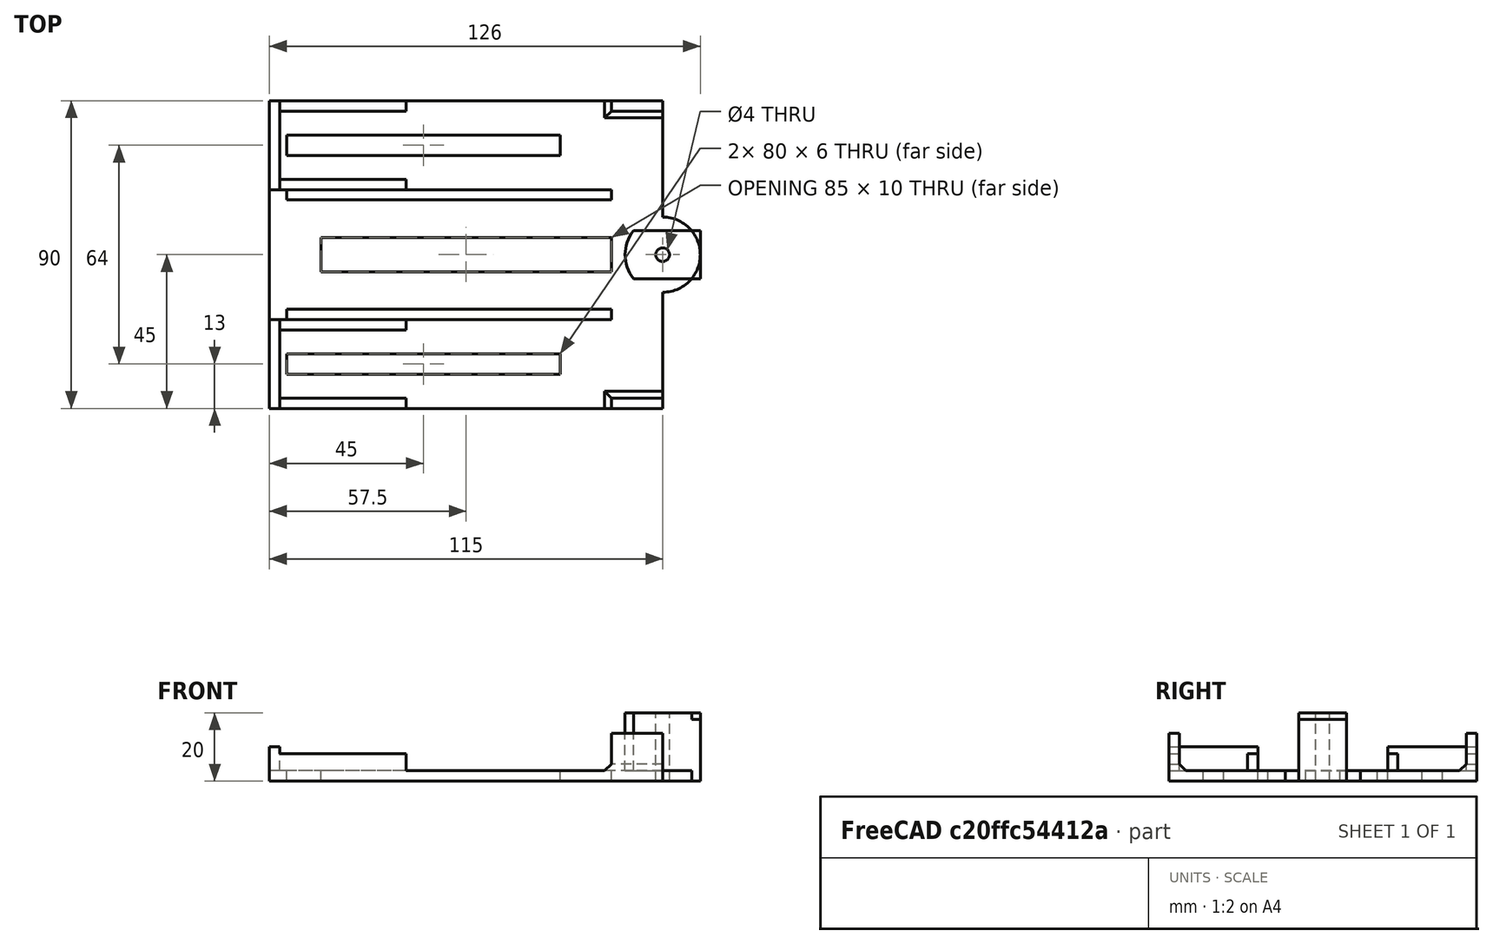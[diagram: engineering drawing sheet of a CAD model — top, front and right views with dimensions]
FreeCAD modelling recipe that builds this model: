
FCSTD DOCUMENT  (FreeCAD 0.18R16131 (Git))
Label: chassis_1
License: All rights reserved
LicenseURL: http://en.wikipedia.org/wiki/All_rights_reserved
objects: Part::Box×18, Part::MultiFuse×10, Part::Cut×9, Part::Cylinder×2, Part::Chamfer×2
note: 41 computed .brp shape members not serialized (recipe doc carries the construction recipe); baked Part::Feature solids carry a one-line shape summary decoded from their .brp

FEATURE [Part::Box] Box  label="Cube"
  AttacherType = Attacher::AttachEngine3D
  Height = 3
  Length = 115
  Width = 90
FEATURE [Part::Box] Box001  label="Cube001"
  AttacherType = Attacher::AttachEngine3D
  Height = 14
  Length = 15
  Placement = pos=(100,0,0) rot=(0,0,1;0rad)
  Width = 3
FEATURE [Part::MultiFuse] Fusion
  Shapes = -> [Box,Box001]
FEATURE [Part::Box] Box002  label="Cube002"
  AttacherType = Attacher::AttachEngine3D
  Height = 14
  Length = 15
  Placement = pos=(100,87,0) rot=(0,0,1;0rad)
  Width = 3
FEATURE [Part::MultiFuse] Fusion001
  Shapes = -> [Fusion,Box002]
FEATURE [Part::Cylinder] Cylinder
  Angle = 360
  AttacherType = Attacher::AttachEngine3D
  Height = 20
  Placement = pos=(115,45,0) rot=(0,0,1;0rad)
  Radius = 11
FEATURE [Part::MultiFuse] Fusion002
  Shapes = -> [Fusion001,Cylinder]
FEATURE [Part::Box] Box003  label="Cube003"
  AttacherType = Attacher::AttachEngine3D
  Height = 10
  Length = 3
  Width = 26
FEATURE [Part::MultiFuse] Fusion003
  Shapes = -> [Fusion002,Box003]
FEATURE [Part::Box] Box004  label="Cube004"
  AttacherType = Attacher::AttachEngine3D
  Height = 10
  Length = 3
  Placement = pos=(0,64,0) rot=(0,0,1;0rad)
  Width = 26
FEATURE [Part::MultiFuse] Fusion004
  Shapes = -> [Fusion003,Box004]
FEATURE [Part::Box] Box005  label="Cube005"
  AttacherType = Attacher::AttachEngine3D
  Height = 8
  Length = 40
  Width = 3
FEATURE [Part::MultiFuse] Fusion005
  Shapes = -> [Fusion004,Box005]
FEATURE [Part::Box] Box006  label="Cube006"
  AttacherType = Attacher::AttachEngine3D
  Height = 8
  Length = 40
  Placement = pos=(0,23,0) rot=(0,0,1;0rad)
  Width = 3
FEATURE [Part::MultiFuse] Fusion006
  Shapes = -> [Fusion005,Box006]
FEATURE [Part::Box] Box007  label="Cube007"
  AttacherType = Attacher::AttachEngine3D
  Height = 8
  Length = 40
  Placement = pos=(0,64,0) rot=(0,0,1;0rad)
  Width = 3
FEATURE [Part::MultiFuse] Fusion007
  Shapes = -> [Fusion006,Box007]
FEATURE [Part::Box] Box008  label="Cube008"
  AttacherType = Attacher::AttachEngine3D
  Height = 8
  Length = 40
  Placement = pos=(0,87,0) rot=(0,0,1;0rad)
  Width = 3
FEATURE [Part::MultiFuse] Fusion008
  Shapes = -> [Fusion007,Box008]
FEATURE [Part::Box] Box009  label="Cube009"
  AttacherType = Attacher::AttachEngine3D
  Height = 18
  Length = 10
  Placement = pos=(116,38,0) rot=(0,0,1;0rad)
  Width = 14
FEATURE [Part::MultiFuse] Fusion009
  Shapes = -> [Fusion008,Box009]
FEATURE [Part::Box] Box010  label="Cube010"
  AttacherType = Attacher::AttachEngine3D
  Height = 17
  Length = 21
  Placement = pos=(105,28,3) rot=(0,0,1;0rad)
  Width = 10
FEATURE [Part::Cut] Cut
  Base = -> Fusion009
  Tool = -> Box010
FEATURE [Part::Box] Box011  label="Cube011"
  AttacherType = Attacher::AttachEngine3D
  Height = 17
  Length = 21
  Placement = pos=(104,52,3) rot=(0,0,1;0rad)
  Width = 10
FEATURE [Part::Cut] Cut001
  Base = -> Cut
  Tool = -> Box011
FEATURE [Part::Box] Box012  label="Cube012"
  AttacherType = Attacher::AttachEngine3D
  Height = 10
  Length = 85
  Placement = pos=(20,40,0) rot=(0,0,1;0rad)
  Width = 10
FEATURE [Part::Cut] Cut002
  Base = -> Cut001
  Tool = -> Box012
FEATURE [Part::Box] Box013  label="Cube013"
  AttacherType = Attacher::AttachEngine3D
  Height = 10
  Length = 95
  Placement = pos=(5,26,0) rot=(0,0,1;0rad)
  Width = 3
FEATURE [Part::Cut] Cut003
  Base = -> Cut002
  Tool = -> Box013
FEATURE [Part::Box] Box014  label="Cube014"
  AttacherType = Attacher::AttachEngine3D
  Height = 10
  Length = 95
  Placement = pos=(5,61,0) rot=(0,0,1;0rad)
  Width = 3
FEATURE [Part::Cut] Cut004
  Base = -> Cut003
  Tool = -> Box014
FEATURE [Part::Box] Box015  label="Cube015"
  AttacherType = Attacher::AttachEngine3D
  Height = 10
  Length = 80
  Placement = pos=(5,10,0) rot=(0,0,1;0rad)
  Width = 6
FEATURE [Part::Cut] Cut005
  Base = -> Cut004
  Tool = -> Box015
FEATURE [Part::Box] Box016  label="Cube016"
  AttacherType = Attacher::AttachEngine3D
  Height = 10
  Length = 80
  Placement = pos=(5,74,0) rot=(0,0,1;0rad)
  Width = 6
FEATURE [Part::Cut] Cut006
  Base = -> Cut005
  Tool = -> Box016
FEATURE [Part::Chamfer] Chamfer
  Base = -> Cut006
  Edges = 2 edges r=2: [Edge179,Edge181]
FEATURE [Part::Chamfer] Chamfer001
  Base = -> Chamfer
  Edges = 2 edges r=2: [Edge24,Edge26]
FEATURE [Part::Box] Box017  label="Cube017"
  AttacherType = Attacher::AttachEngine3D
  Height = 10
  Length = 5
  Placement = pos=(15,40,0) rot=(0,0,1;0rad)
  Width = 10
FEATURE [Part::Cut] Cut007
  Base = -> Chamfer001
  Tool = -> Box017
FEATURE [Part::Cylinder] Cylinder001
  Angle = 360
  AttacherType = Attacher::AttachEngine3D
  Height = 30
  Placement = pos=(115,45,0) rot=(0,0,1;0rad)
  Radius = 2
FEATURE [Part::Cut] Cut008
  Base = -> Cut007
  Tool = -> Cylinder001
